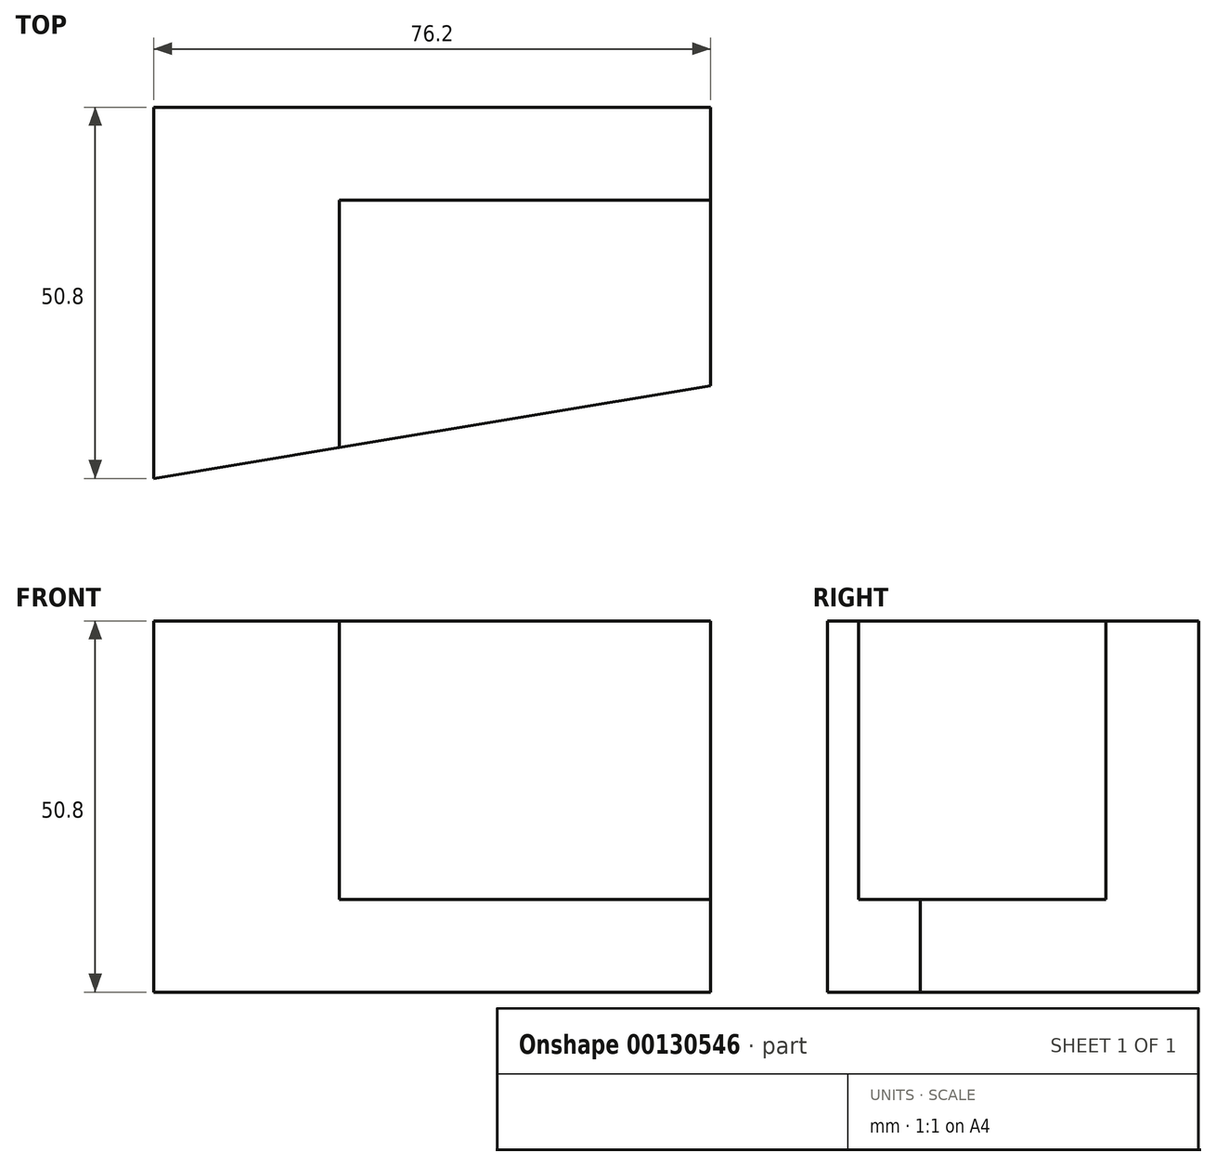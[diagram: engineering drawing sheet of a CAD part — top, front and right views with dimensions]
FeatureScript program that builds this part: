
annotation { "Feature Type Name" : "Feature", "Feature Type Description" : "" }
export const myFeature = defineFeature(function(context is Context, id is Id, definition is map)
    precondition{}
    {
        {
            var Q0;
            Q0=qCreatedBy(makeId("Front.planeOp"),FACE);
            var sketch = newSketch(context, id + "F0", { "sketchPlane" : qUnion([Q0])});
            skLineSegment(sketch, "E0", {"start": v(0, 0) * mm, "end": v(76.2, 0) * mm});
            skLineSegment(sketch, "E1", {"start": v(0, 0) * mm, "end": v(0, 50.8) * mm});
            skLineSegment(sketch, "E2", {"start": v(0, 50.8) * mm, "end": v(76.2, 50.8) * mm});
            skLineSegment(sketch, "E3", {"start": v(76.2, 50.8) * mm, "end": v(76.2, 0) * mm});
            skLineSegment(sketch, "E4", {"start": v(76.2, 12.7) * mm, "end": v(25.4, 12.7) * mm});
            skLineSegment(sketch, "E5", {"start": v(25.4, 12.7) * mm, "end": v(25.4, 50.8) * mm});
            skSolve(sketch);
        }
        {
            var Q0;
            Q0=qCreatedBy(makeId("Top.planeOp"),FACE);
            var sketch = newSketch(context, id + "F1", { "sketchPlane" : qUnion([Q0])});
            skLineSegment(sketch, "E6", {"start": v(0, 0) * mm, "end": v(0, 50.8) * mm});
            skLineSegment(sketch, "E7", {"start": v(0, 50.8) * mm, "end": v(76.2, 50.8) * mm});
            skLineSegment(sketch, "E8", {"start": v(76.2, 50.8) * mm, "end": v(76.2, 12.7) * mm});
            skLineSegment(sketch, "E9", {"start": v(76.2, 12.7) * mm, "end": v(0, 0) * mm});
            skLineSegment(sketch, "E10", {"start": v(76.2, 38.1) * mm, "end": v(25.4, 38.1) * mm});
            skLineSegment(sketch, "E11", {"start": v(25.4, 38.1) * mm, "end": v(25.4, 4.23) * mm});
            skSolve(sketch);
        }
        {
            var Q0;
            {var subQ2=sQuery(id+"F1.wireOp",EDGE,"E6");Q0=makeQuery(id+"F1.imprint","IMPRINT",FACE,{"disambiguationData":[TD([[makeQuery(id+"F1.imprint","IMPRINT",EDGE,{"derivedFrom":subQ2}),-1.0]])]});}
            var Q1;
            {var subQ3=sQuery(id+"F1.wireOp",EDGE,"E10");Q1=makeQuery(id+"F1.imprint","IMPRINT",FACE,{"disambiguationData":[TD([[makeQuery(id+"F1.imprint","IMPRINT",EDGE,{"derivedFrom":subQ3}),1.0]])]});}
            extrude(context, id + "F2", {"entities" : qUnion([Q0, Q1]), "depth" : 50.8 * mm});
        }
        {
            var Q0;
            {var subQ4=sQuery(id+"F0.wireOp",EDGE,"E4");Q0=makeQuery(id+"F0.imprint","IMPRINT",FACE,{"disambiguationData":[TD([[makeQuery(id+"F0.imprint","IMPRINT",EDGE,{"derivedFrom":subQ4}),-1.0]])]});}
            extrude(context, id + "F3", {"entities" : qUnion([Q0]), "operationType" : NewBodyOperationType.REMOVE, "oppositeDirection" : true, "depth" : 38.1 * mm});
        }
    });
